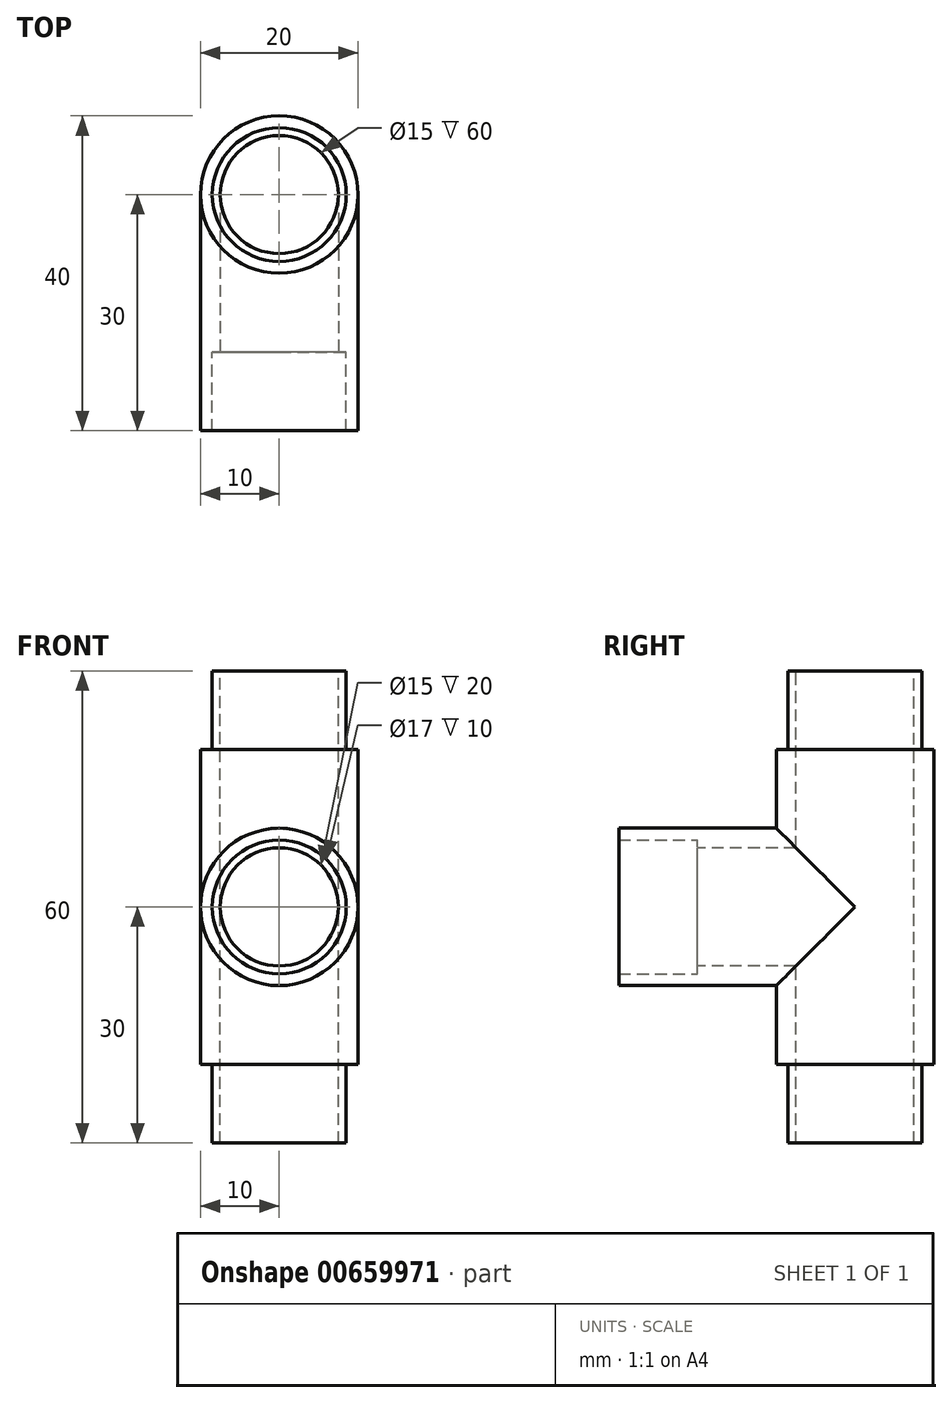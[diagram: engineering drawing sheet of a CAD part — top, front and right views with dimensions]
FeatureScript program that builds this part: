
annotation { "Feature Type Name" : "Feature", "Feature Type Description" : "" }
export const myFeature = defineFeature(function(context is Context, id is Id, definition is map)
    precondition{}
    {
        {
            var Q0;
            Q0=qCreatedBy(makeId("Top.planeOp"),FACE);
            var sketch = newSketch(context, id + "F0", { "sketchPlane" : qUnion([Q0])});
            skCircle(sketch, "E0", {"center": v(0, 0) * mm, "radius": 10 * mm});
            skCircle(sketch, "E1", {"center": v(0, 0) * mm, "radius": 8.5 * mm});
            skCircle(sketch, "E2", {"center": v(0, 0) * mm, "radius": 7.5 * mm});
            skSolve(sketch);
        }
        {
            var Q0;
            Q0=qCreatedBy(makeId("Right.planeOp"),FACE);
            var sketch = newSketch(context, id + "F1", { "sketchPlane" : qUnion([Q0])});
            skLineSegment(sketch, "E3", {"start": v(0, 0) * mm, "end": v(0, 30) * mm});
            skLineSegment(sketch, "E4", {"start": v(0, 0) * mm, "end": v(0, -30) * mm});
            skSolve(sketch);
        }
        {
            var Q0;
            Q0=makeQuery(id+"F0.imprint","IMPRINT",FACE,{"disambiguationData":[TD([[makeQuery(id+"F0.imprint","IMPRINT",EDGE,{"derivedFrom":sQuery(id+"F0.wireOp",EDGE,"E1")}),1.0]])]});
            var Q1;
            Q1=sQuery(id+"F1.wireOp",EDGE,"E3");
            sweep(context, id + "F2", {"profiles" : qUnion([Q0]), "path" : qUnion([Q1])});
        }
        {
            var Q0;
            Q0=qCreatedBy(makeId("Front.planeOp"),FACE);
            var sketch = newSketch(context, id + "F3", { "sketchPlane" : qUnion([Q0])});
            skLineSegment(sketch, "E5", {"start": v(0, 0) * mm, "end": v(0, 20) * mm});
            skLineSegment(sketch, "E6", {"start": v(0, 0) * mm, "end": v(0, -20) * mm});
            skSolve(sketch);
        }
        {
            var Q0;
            Q0=makeQuery(id+"F2.opSweep","CAP_FACE",FACE,{"disambiguationData":[OSD([sQuery(id+"F0.wireOp",EDGE,"E1"),sQuery(id+"F0.wireOp",EDGE,"E2"),sQuery(id+"F1.wireOp",VERTEX,"E3.start")])],"isStart":true});
            var Q1;
            Q1 = qConstructionFilter(qBodyType(qCreatedBy(id + "F1" ,EDGE), BodyType.WIRE), ConstructionObject.NO);
            sweep(context, id + "F4", {"operationType" : NewBodyOperationType.ADD, "profiles" : qUnion([Q0]), "path" : qUnion([Q1])});
        }
        {
            var Q0;
            Q0=makeQuery(id+"F0.imprint","IMPRINT",FACE,{"disambiguationData":[TD([[makeQuery(id+"F0.imprint","IMPRINT",EDGE,{"derivedFrom":sQuery(id+"F0.wireOp",EDGE,"E0")}),1.0]])]});
            var Q1;
            Q1 = qConstructionFilter(qBodyType(qCreatedBy(id + "F3" ,EDGE), BodyType.WIRE), ConstructionObject.NO);
            sweep(context, id + "F5", {"operationType" : NewBodyOperationType.ADD, "profiles" : qUnion([Q0]), "path" : qUnion([Q1])});
        }
        {
            var Q0;
            Q0=qCreatedBy(makeId("Front.planeOp"),FACE);
            var sketch = newSketch(context, id + "F6", { "sketchPlane" : qUnion([Q0])});
            skCircle(sketch, "E7", {"center": v(0, 0) * mm, "radius": 10 * mm});
            skSolve(sketch);
        }
        {
            var Q0;
            Q0=qCreatedBy(makeId("Right.planeOp"),FACE);
            var sketch = newSketch(context, id + "F7", { "sketchPlane" : qUnion([Q0])});
            skLineSegment(sketch, "E8", {"start": v(0, 0) * mm, "end": v(-30, 0) * mm});
            skSolve(sketch);
        }
        {
            var Q0;
            Q0 = qSketchRegion(id + "F6", true);
            var Q1;
            Q1=sQuery(id+"F6.wireOp",EDGE,"E7");
            var Q2;
            Q2=sQuery(id+"F7.wireOp",EDGE,"E8");
            sweep(context, id + "F8", {"operationType" : NewBodyOperationType.REMOVE, "profiles" : qUnion([Q0]), "surfaceProfiles" : qUnion([Q1]), "path" : qUnion([Q2])});
        }
        {
            var Q0;
            Q0=makeQuery(id+"F6.imprint","IMPRINT",FACE,{"disambiguationData":[TD([[makeQuery(id+"F6.imprint","IMPRINT",EDGE,{"derivedFrom":sQuery(id+"F6.wireOp",EDGE,"E7")}),1.0]])]});
            var sketch = newSketch(context, id + "F9", { "sketchPlane" : qUnion([Q0])});
            skCircle(sketch, "E9", {"center": v(0, 0) * mm, "radius": 7.5 * mm});
            skSolve(sketch);
        }
        {
            var Q0;
            Q0 = qSketchRegion(id + "F6", true);
            var Q1;
            Q1 = qConstructionFilter(qBodyType(qCreatedBy(id + "F7" ,EDGE), BodyType.WIRE), ConstructionObject.NO);
            sweep(context, id + "F10", {"operationType" : NewBodyOperationType.ADD, "profiles" : qUnion([Q0]), "path" : qUnion([Q1])});
        }
        {
            var Q0;
            Q0 = qSketchRegion(id + "F9", true);
            var Q1;
            Q1 = qConstructionFilter(qBodyType(qCreatedBy(id + "F7" ,EDGE), BodyType.WIRE), ConstructionObject.NO);
            sweep(context, id + "F11", {"operationType" : NewBodyOperationType.REMOVE, "profiles" : qUnion([Q0]), "path" : qUnion([Q1])});
        }
        {
            var Q0;
            Q0=qCreatedBy(makeId("Top.planeOp"),FACE);
            var sketch = newSketch(context, id + "F12", { "sketchPlane" : qUnion([Q0])});
            skCircle(sketch, "E10", {"center": v(0, 0) * mm, "radius": 7.5 * mm});
            skSolve(sketch);
        }
        {
            var Q0;
            Q0=qCreatedBy(makeId("Top.planeOp"),FACE);
            var sketch = newSketch(context, id + "F13", { "sketchPlane" : qUnion([Q0])});
            skLineSegment(sketch, "E11", {"start": v(0, -30) * mm, "end": v(0, -20) * mm});
            skSolve(sketch);
        }
        {
            var Q0;
            Q0=makeQuery(id+"F10.opSweep","CAP_FACE",FACE,{"disambiguationData":[OSD([sQuery(id+"F6.wireOp",EDGE,"E7"),sQuery(id+"F7.wireOp",VERTEX,"E8.end")])],"isStart":false});
            var sketch = newSketch(context, id + "F14", { "sketchPlane" : qUnion([Q0])});
            skCircle(sketch, "E12", {"center": v(0, 0) * mm, "radius": 8.5 * mm});
            skCircle(sketch, "E13", {"center": v(0, 0) * mm, "radius": 7.5 * mm});
            skSolve(sketch);
        }
        {
            var Q0;
            Q0 = qSketchRegion(id + "F14", true);
            var Q1;
            Q1 = qConstructionFilter(qBodyType(qCreatedBy(id + "F13" ,EDGE), BodyType.WIRE), ConstructionObject.NO);
            sweep(context, id + "F15", {"operationType" : NewBodyOperationType.REMOVE, "profiles" : qUnion([Q0]), "path" : qUnion([Q1])});
        }
        {
            var Q0;
            Q0 = qSketchRegion(id + "F12", true);
            var Q1;
            Q1 = qConstructionFilter(qBodyType(qCreatedBy(id + "F3" ,EDGE), BodyType.WIRE), ConstructionObject.NO);
            sweep(context, id + "F16", {"operationType" : NewBodyOperationType.REMOVE, "profiles" : qUnion([Q0]), "path" : qUnion([Q1])});
        }
        {
            var Q0;
            Q0 = qSketchRegion(id + "F12", true);
            var Q1;
            Q1=makeQuery(id+"F4.opSweep","CAP_EDGE",EDGE,{"disambiguationData":[OSD([sQuery(id+"F0.wireOp",EDGE,"E2"),sQuery(id+"F1.wireOp",VERTEX,"E3.start"),sQuery(id+"F1.wireOp",VERTEX,"E4.end")])],"isStart":false});
            var Q2;
            Q2 = qConstructionFilter(qBodyType(qCreatedBy(id + "F1" ,EDGE), BodyType.WIRE), ConstructionObject.NO);
            sweep(context, id + "F17", {"operationType" : NewBodyOperationType.REMOVE, "profiles" : qUnion([Q0]), "surfaceProfiles" : qUnion([Q1]), "path" : qUnion([Q2])});
        }
    });
